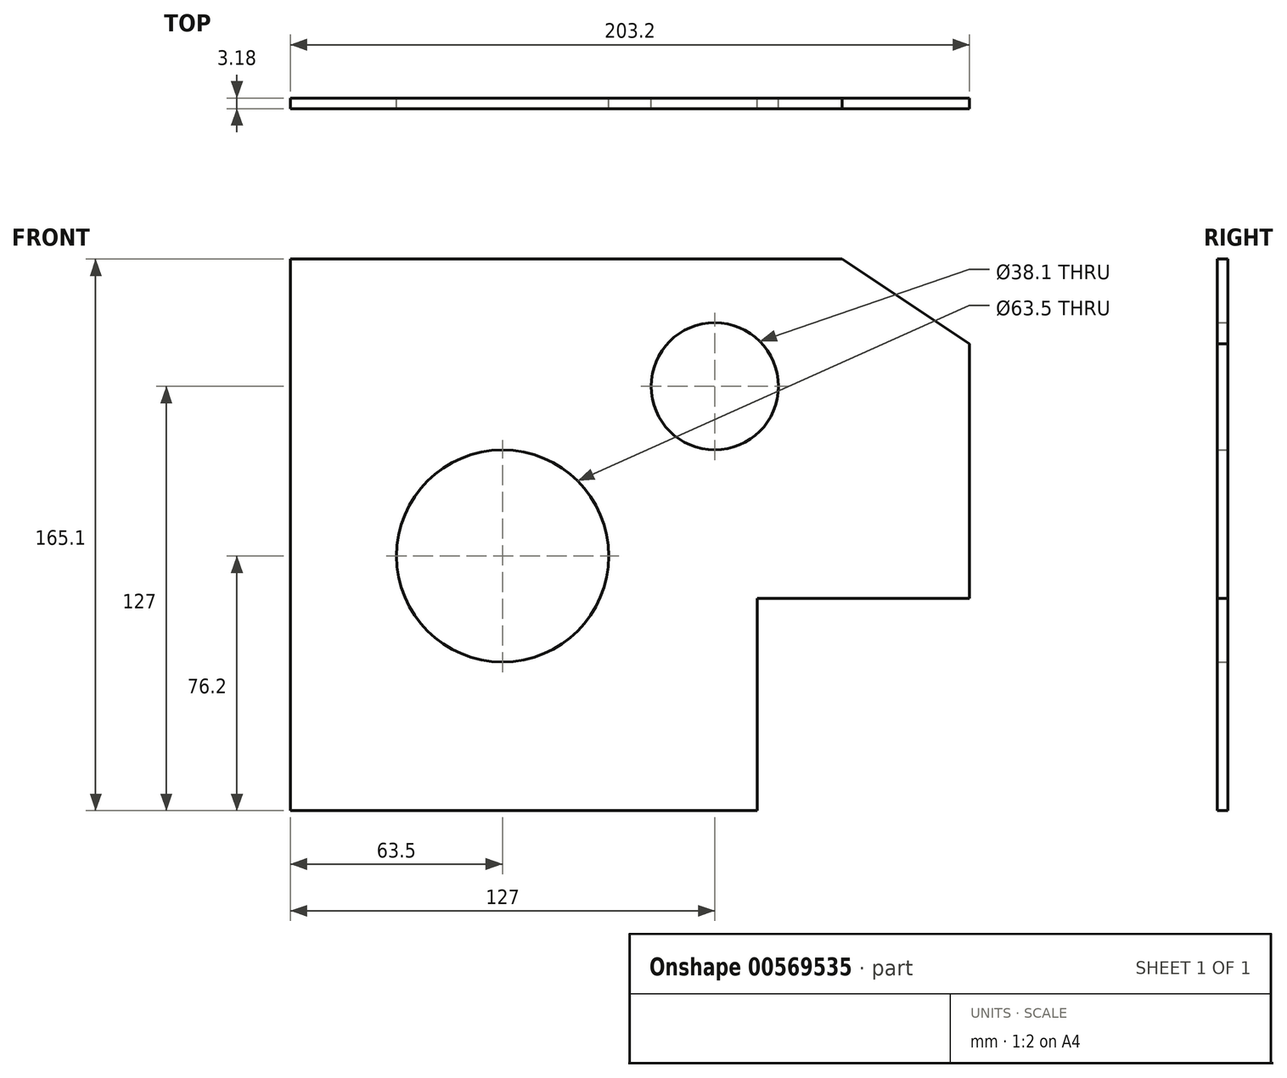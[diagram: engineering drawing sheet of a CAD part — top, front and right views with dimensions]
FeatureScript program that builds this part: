
annotation { "Feature Type Name" : "Feature", "Feature Type Description" : "" }
export const myFeature = defineFeature(function(context is Context, id is Id, definition is map)
    precondition{}
    {
        {
            var Q0;
            Q0=qCreatedBy(makeId("Front.planeOp"),FACE);
            var sketch = newSketch(context, id + "F0", { "sketchPlane" : qUnion([Q0])});
            skLineSegment(sketch, "E0.bottom", {"start": v(0, 0) * mm, "end": v(139.7, 0) * mm});
            skLineSegment(sketch, "E0.top", {"start": v(0, 165.1) * mm, "end": v(127, 165.1) * mm});
            skLineSegment(sketch, "E0.left", {"start": v(0, 0) * mm, "end": v(0, 165.1) * mm});
            skLineSegment(sketch, "E1.top", {"start": v(203.2, 63.5) * mm, "end": v(139.7, 63.5) * mm});
            skLineSegment(sketch, "E1.right", {"start": v(139.7, 0) * mm, "end": v(139.7, 63.5) * mm});
            skLineSegment(sketch, "E2.bottom", {"start": v(0, 0) * mm, "end": v(63.5, 0) * mm});
            skLineSegment(sketch, "E2.left", {"start": v(0, 0) * mm, "end": v(0, 76.2) * mm});
            skLineSegment(sketch, "E3.left", {"start": v(0, 165.1) * mm, "end": v(0, 127) * mm});
            skCircle(sketch, "E4", {"center": v(127, 127) * mm, "radius": 19.05 * mm});
            skCircle(sketch, "E5", {"center": v(63.5, 76.2) * mm, "radius": 31.75 * mm});
            skLineSegment(sketch, "E6", {"start": v(0, 165.1) * mm, "end": v(165.1, 165.1) * mm});
            skLineSegment(sketch, "E7", {"start": v(203.2, 63.5) * mm, "end": v(203.2, 139.7) * mm});
            skLineSegment(sketch, "E8", {"start": v(165.1, 165.1) * mm, "end": v(203.2, 139.7) * mm});
            skSolve(sketch);
        }
        {
            var Q0;
            Q0=makeQuery(id+"F0.imprint","IMPRINT",FACE,{"disambiguationData":[TD([[makeQuery(id+"F0.imprint","IMPRINT",EDGE,{"derivedFrom":sQuery(id+"F0.wireOp",EDGE,"E0.bottom")}),1.0]])]});
            extrude(context, id + "F1", {"entities" : qUnion([Q0]), "depth" : 3.17 * mm, "offsetDistance" : 25.4 * mm});
        }
    });
